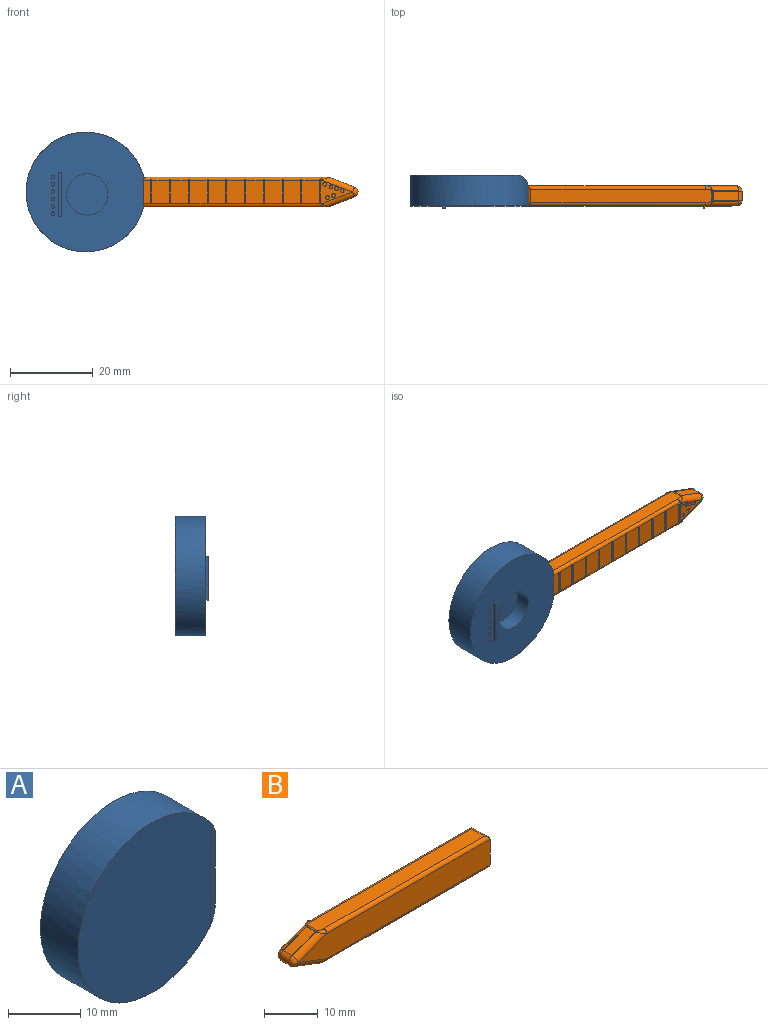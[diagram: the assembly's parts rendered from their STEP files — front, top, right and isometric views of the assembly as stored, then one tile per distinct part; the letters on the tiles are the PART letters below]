
ASSEMBLY  parts=2 mates=1
PART A: 24 faces, bbox 28.4x8x28.8 mm
  f0: plane 28.82x28.36mm, normal (0,1,0), area 560.4mm2, adj f1,f2,f5,f7,f8,f9,f10,f12
  f1: plane 7.18x4.83mm, normal (1,0,0), area 34.7mm2, adj f0,f2,f4
  f2: cylinder r=14.41mm len=28.82mm, axis (0,1,0), area 605.3mm2, adj f0,f1,f3,f4
  f3: plane 28.82x25.82mm, normal (0,-1,0), area 616.3mm2, adj f2,f4
  f4: cylinder r=2.54mm len=17.59mm, axis (0,0,-1), area 46.8mm2, adj f1,f2,f3
  f5: cylinder r=4.98mm len=9.96mm, axis (0,1,0), area 119.2mm2, adj f0,f6
  f6: plane 9.96x9.96mm, normal (0,1,0), area 77.9mm2, adj f5
  f7: plane 10.67x0.64mm, normal (1,0,0), area 6.8mm2, adj f0,f8,f10,f11
  f8: plane 0.76x0.64mm, normal (0,0,1), area 0.5mm2, adj f0,f7,f9,f11
  f9: plane 10.67x0.64mm, normal (-1,0,0), area 6.8mm2, adj f0,f8,f10,f11
  f10: plane 0.76x0.64mm, normal (0,0,-1), area 0.5mm2, adj f0,f7,f9,f11
  f11: plane 10.67x0.76mm, normal (0,1,0), area 8.1mm2, adj f7,f8,f9,f10
  f12: cylinder r=0.44mm len=0.87mm, axis (0,1,0), area 1.2mm2, adj f0,f13
  f13: plane 0.87x0.87mm, normal (0,1,0), area 0.6mm2, adj f12
  f14: cylinder r=0.44mm len=0.87mm, axis (0,1,0), area 1.2mm2, adj f0,f15
  f15: plane 0.87x0.87mm, normal (0,1,0), area 0.6mm2, adj f14
  f16: cylinder r=0.44mm len=0.87mm, axis (0,1,0), area 1.2mm2, adj f0,f17
  f17: plane 0.87x0.87mm, normal (0,1,0), area 0.6mm2, adj f16
  f18: cylinder r=0.44mm len=0.87mm, axis (0,1,0), area 1.2mm2, adj f0,f19
  f19: plane 0.87x0.87mm, normal (0,1,0), area 0.6mm2, adj f18
  f20: cylinder r=0.44mm len=0.87mm, axis (0,1,0), area 1.2mm2, adj f0,f21
  f21: plane 0.87x0.87mm, normal (0,1,0), area 0.6mm2, adj f20
  f22: cylinder r=0.44mm len=0.87mm, axis (0,1,0), area 1.2mm2, adj f0,f23
  f23: plane 0.87x0.87mm, normal (0,1,0), area 0.6mm2, adj f22
PART B: 94 faces, bbox 51.6x5.5x8.1 mm
  f0: plane 5.62x0.54mm, normal (1,0,0), area 3mm2, adj f1,f3,f50,f52,f79
  f1: plane 0.54x0.26mm, normal (0,0,1), area 0.1mm2, adj f0,f2,f52,f79
  f2: plane 5.62x0.54mm, normal (-1,0,0), area 3mm2, adj f1,f3,f50,f52,f79
  f3: plane 0.53x0.25mm, normal (0,0,-1), area 0.1mm2, adj f0,f2,f50,f79
  f4: plane 5.62x0.24mm, normal (1,0,0), area 1.3mm2, adj f5,f7,f8,f50,f52
  f5: plane 0.26x0.24mm, normal (0,0,1), area 0.1mm2, adj f4,f6,f8,f52
  f6: plane 5.62x0.24mm, normal (-1,0,0), area 1.3mm2, adj f5,f7,f8,f50,f52
  f7: plane 0.25x0.23mm, normal (0,0,-1), area 0.1mm2, adj f4,f6,f8,f50
  f8: plane 5.61x0.25mm, normal (0,1,0), area 1.4mm2, adj f4,f5,f6,f7
  f9: plane 5.62x0.24mm, normal (1,0,0), area 1.3mm2, adj f10,f12,f13,f50,f52
  f10: plane 0.26x0.24mm, normal (0,0,1), area 0.1mm2, adj f9,f11,f13,f52
  f11: plane 5.62x0.24mm, normal (-1,0,0), area 1.3mm2, adj f10,f12,f13,f50,f52
  f12: plane 0.25x0.23mm, normal (0,0,-1), area 0.1mm2, adj f9,f11,f13,f50
  f13: plane 5.61x0.25mm, normal (0,1,0), area 1.4mm2, adj f9,f10,f11,f12
  f14: plane 5.62x0.24mm, normal (1,0,0), area 1.3mm2, adj f15,f17,f18,f50,f52
  f15: plane 0.26x0.24mm, normal (0,0,1), area 0.1mm2, adj f14,f16,f18,f52
  f16: plane 5.62x0.24mm, normal (-1,0,0), area 1.3mm2, adj f15,f17,f18,f50,f52
  f17: plane 0.25x0.23mm, normal (0,0,-1), area 0.1mm2, adj f14,f16,f18,f50
  f18: plane 5.61x0.25mm, normal (0,1,0), area 1.4mm2, adj f14,f15,f16,f17
  f19: plane 5.62x0.24mm, normal (1,0,0), area 1.3mm2, adj f20,f22,f23,f50,f52
  f20: plane 0.26x0.24mm, normal (0,0,1), area 0.1mm2, adj f19,f21,f23,f52
  f21: plane 5.62x0.24mm, normal (-1,0,0), area 1.3mm2, adj f20,f22,f23,f50,f52
  f22: plane 0.25x0.23mm, normal (0,0,-1), area 0.1mm2, adj f19,f21,f23,f50
  f23: plane 5.61x0.25mm, normal (0,1,0), area 1.4mm2, adj f19,f20,f21,f22
  f24: plane 5.62x0.24mm, normal (1,0,0), area 1.3mm2, adj f25,f27,f28,f50,f52
  f25: plane 0.26x0.24mm, normal (0,0,1), area 0.1mm2, adj f24,f26,f28,f52
  f26: plane 5.62x0.24mm, normal (-1,0,0), area 1.3mm2, adj f25,f27,f28,f50,f52
  f27: plane 0.25x0.23mm, normal (0,0,-1), area 0.1mm2, adj f24,f26,f28,f50
  f28: plane 5.61x0.25mm, normal (0,1,0), area 1.4mm2, adj f24,f25,f26,f27
  f29: plane 5.62x0.24mm, normal (1,0,0), area 1.3mm2, adj f30,f32,f33,f50,f52
  f30: plane 0.26x0.24mm, normal (0,0,1), area 0.1mm2, adj f29,f31,f33,f52
  f31: plane 5.62x0.24mm, normal (-1,0,0), area 1.3mm2, adj f30,f32,f33,f50,f52
  f32: plane 0.25x0.23mm, normal (0,0,-1), area 0.1mm2, adj f29,f31,f33,f50
  f33: plane 5.61x0.25mm, normal (0,1,0), area 1.4mm2, adj f29,f30,f31,f32
  f34: plane 5.62x0.24mm, normal (1,0,0), area 1.3mm2, adj f35,f37,f38,f50,f52
  f35: plane 0.26x0.24mm, normal (0,0,1), area 0.1mm2, adj f34,f36,f38,f52
  f36: plane 5.62x0.24mm, normal (-1,0,0), area 1.3mm2, adj f35,f37,f38,f50,f52
  f37: plane 0.25x0.23mm, normal (0,0,-1), area 0.1mm2, adj f34,f36,f38,f50
  f38: plane 5.61x0.25mm, normal (0,1,0), area 1.4mm2, adj f34,f35,f36,f37
  f39: plane 5.62x0.24mm, normal (1,0,0), area 1.3mm2, adj f40,f42,f43,f50,f52
  f40: plane 0.26x0.24mm, normal (0,0,1), area 0.1mm2, adj f39,f41,f43,f52
  f41: plane 5.62x0.24mm, normal (-1,0,0), area 1.3mm2, adj f40,f42,f43,f50,f52
  f42: plane 0.25x0.23mm, normal (0,0,-1), area 0.1mm2, adj f39,f41,f43,f50
  f43: plane 5.61x0.25mm, normal (0,1,0), area 1.4mm2, adj f39,f40,f41,f42
  f44: plane 5.69x4.83mm, normal (1,0,0), area 27.5mm2, adj f49,f50,f53,f56
  f45: plane 43.46x3.3mm, normal (0,0,1), area 143.2mm2, adj f51,f52,f53,f57,f60,f65
  f46: plane 6.15x2.34mm, normal (-0.35,0,0.93), area 15mm2, adj f59,f60,f67,f68
  f47: plane 6.15x2.34mm, normal (-0.35,0,-0.93), area 15mm2, adj f62,f67,f69,f72
  f48: plane 43.46x3.3mm, normal (0,0,-1), area 143.2mm2, adj f54,f55,f56,f61,f69,f73
  f49: plane 50.37x5.69mm, normal (0,-1,0), area 265.3mm2, adj f44,f51,f54,f68,f72
  f50: plane 50.37x5.69mm, normal (0,1,0), area 247.5mm2, adj f0,f2,f3,f4,f6,f7,f9,f11
  f51: cylinder r=0.76mm len=42.88mm, axis (1,0,0), area 50.9mm2, adj f45,f49,f53,f65
  f52: cylinder r=0.76mm len=42.88mm, axis (-1,0,0), area 50.8mm2, adj f0,f1,f2,f4,f5,f6,f9,f10
  f53: cylinder r=0.76mm len=4.83mm, axis (0,-1,0), area 4.9mm2, adj f44,f45,f51,f52
  f54: cylinder r=0.76mm len=42.88mm, axis (-1,0,0), area 50.9mm2, adj f48,f49,f56,f73
  f55: cylinder r=0.76mm len=42.88mm, axis (1,0,0), area 50.9mm2, adj f48,f50,f56,f61
  f56: cylinder r=0.76mm len=4.83mm, axis (0,1,0), area 4.9mm2, adj f44,f48,f54,f55
  f57: bspline ~1.97x1.28mm, area 1.3mm2, adj f45,f52,f58,f59
  f58: bspline ~0.53x0.52mm, area 0.1mm2, adj f57,f59,f60
  f59: cylinder r=1.27mm len=7.94mm, axis (-0.93,0,-0.35), area 14.4mm2, adj f46,f50,f57,f58,f63
  f60: cylinder r=1.27mm len=2.65mm, axis (0,1,0), area 1.1mm2, adj f45,f46,f58,f64
  f61: bspline ~1.97x1.28mm, area 1.3mm2, adj f48,f55,f62,f66
  f62: cylinder r=1.27mm len=7.94mm, axis (0.93,0,-0.35), area 14.4mm2, adj f47,f50,f61,f63,f66
  f63: sphere r=1.27mm, area 2.7mm2, adj f59,f62,f67
  f64: bspline ~0.53x0.52mm, area 0.1mm2, adj f60,f65,f68
  f65: bspline ~1.97x1.28mm, area 1.3mm2, adj f45,f51,f64,f68
  f66: bspline ~0.53x0.52mm, area 0.1mm2, adj f61,f62,f69
  f67: cylinder r=1.27mm len=2.37mm, axis (0,-1,0), area 7mm2, adj f46,f47,f63,f70
  f68: cylinder r=1.27mm len=7.94mm, axis (0.93,0,0.35), area 14.4mm2, adj f46,f49,f64,f65,f70
  f69: cylinder r=1.27mm len=2.65mm, axis (0,1,0), area 1.1mm2, adj f47,f48,f66,f71
  f70: sphere r=1.27mm, area 2.7mm2, adj f67,f68,f72
  f71: bspline ~0.53x0.52mm, area 0.1mm2, adj f69,f72,f73
  f72: cylinder r=1.27mm len=7.94mm, axis (-0.93,0,0.35), area 14.4mm2, adj f47,f49,f70,f71,f73
  f73: bspline ~1.97x1.28mm, area 1.3mm2, adj f48,f54,f71,f72
  f74: plane 5.62x0.24mm, normal (1,0,0), area 1.3mm2, adj f50,f52,f75,f77,f78
  f75: plane 0.26x0.24mm, normal (0,0,1), area 0.1mm2, adj f52,f74,f76,f78
  f76: plane 5.62x0.24mm, normal (-1,0,0), area 1.3mm2, adj f50,f52,f75,f77,f78
  f77: plane 0.25x0.23mm, normal (0,0,-1), area 0.1mm2, adj f50,f74,f76,f78
  f78: plane 5.61x0.25mm, normal (0,1,0), area 1.4mm2, adj f74,f75,f76,f77
  f79: plane 5.61x0.25mm, normal (0,1,0), area 1.4mm2, adj f0,f1,f2,f3
  f80: cylinder r=0.44mm len=0.89mm, axis (0,1,0), area 2.1mm2, adj f50,f81
  f81: plane 0.89x0.89mm, normal (0,1,0), area 0.6mm2, adj f80
  f82: cylinder r=0.04mm len=0.74mm, axis (0,1,0), area 0.2mm2, adj f84,f85
  f83: cylinder r=0.44mm len=0.89mm, axis (0,1,0), area 2.1mm2, adj f50,f84
  f84: plane 0.89x0.89mm, normal (0,1,0), area 0.6mm2, adj f82,f83
  f85: plane 0.09x0.09mm, normal (0,1,0), area 0mm2, adj f82
  f86: cylinder r=0.44mm len=0.89mm, axis (0,1,0), area 2.1mm2, adj f50,f87
  f87: plane 0.89x0.89mm, normal (0,1,0), area 0.6mm2, adj f86
  f88: cylinder r=0.44mm len=0.89mm, axis (0,1,0), area 2.1mm2, adj f50,f89
  f89: plane 0.89x0.89mm, normal (0,1,0), area 0.6mm2, adj f88
  f90: cylinder r=0.44mm len=0.89mm, axis (0,1,0), area 2.1mm2, adj f50,f91
  f91: plane 0.89x0.89mm, normal (0,1,0), area 0.6mm2, adj f90
  f92: cylinder r=0.44mm len=0.89mm, axis (0,1,0), area 2.1mm2, adj f50,f93
  f93: plane 0.89x0.89mm, normal (0,1,0), area 0.6mm2, adj f92
PLACE A rot(axis=(-1,0,0),180deg) t=(-16.88,-19.45,38.96)mm
PLACE B rot(axis=(0,0,1),180deg) t=(-24.72,-19.45,-5.45)mm
MATE fastened B.f44 <-> A.f1  axis (-1,0,0) through (-36.87,-19.45,10.9)mm
